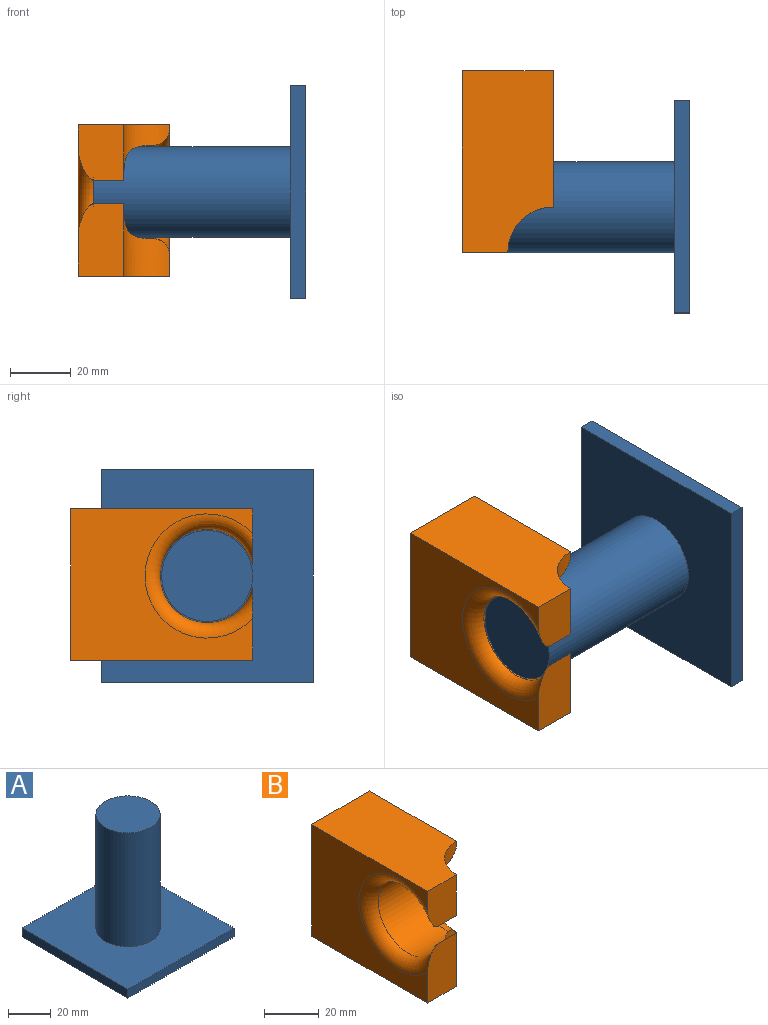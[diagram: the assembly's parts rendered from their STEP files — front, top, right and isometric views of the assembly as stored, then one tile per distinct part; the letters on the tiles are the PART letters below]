
ASSEMBLY  parts=2 mates=1
PART A: 8 faces, bbox 70x70x70 mm
  f0: plane 70x5mm, normal (0,-1,0), area 350mm2, adj f1,f3,f4,f5
  f1: plane 70x5mm, normal (1,0,0), area 350mm2, adj f0,f2,f4,f5
  f2: plane 70x5mm, normal (0,1,0), area 350mm2, adj f1,f3,f4,f5
  f3: plane 70x5mm, normal (-1,0,0), area 350mm2, adj f0,f2,f4,f5
  f4: plane 70x70mm, normal (0,0,1), area 4193.1mm2, adj f0,f1,f2,f3,f6
  f5: plane 70x70mm, normal (0,0,-1), area 4900mm2, adj f0,f1,f2,f3
  f6: cylinder r=15mm len=65mm, axis (0,0,-1), area 6126.1mm2, adj f4,f7
  f7: plane 30x30mm, normal (0,0,1), area 706.9mm2, adj f6
PART B: 12 faces, bbox 30x70.2x53.9 mm
  f0: cylinder r=15mm len=18.27mm, axis (0,0,-1), area 199.7mm2, adj f1,f2,f7,f9,f11
  f1: plane 50x45mm, normal (1,0,0), area 1589.9mm2, adj f0,f3,f4,f7,f8,f11
  f2: plane 18.27x15mm, normal (0,-1,0), area 260.1mm2, adj f0,f5,f7,f9,f10
  f3: cylinder r=15mm len=23.92mm, axis (0,0,-1), area 332.8mm2, adj f1,f6,f8,f9,f11
  f4: plane 50x30mm, normal (0,1,0), area 1500mm2, adj f1,f5,f7,f8
  f5: plane 60x50mm, normal (-1,0,0), area 1785.3mm2, adj f2,f4,f6,f7,f8,f10
  f6: plane 23.92x15mm, normal (0,-1,0), area 344.9mm2, adj f3,f5,f8,f9,f10
  f7: plane 60x30mm, normal (0,0,1), area 1623.3mm2, adj f0,f1,f2,f4,f5
  f8: plane 60x30mm, normal (0,0,-1), area 1623.3mm2, adj f1,f3,f4,f5,f6
  f9: cylinder r=15.5mm len=31mm, axis (1,0,0), area 1480.7mm2, adj f0,f2,f3,f6,f10,f11
  f10: torus R=20.5mm, axis (-1,0,0), area 718.4mm2, adj f2,f5,f6,f9
  f11: torus R=20.5mm, axis (-1,0,0), area 430.3mm2, adj f0,f1,f3,f9
PLACE A rot(axis=(0,-1,0),90deg) t=(49.75,-21.28,34.13)mm
PLACE B at identity
MATE revolute A.f6 <-> B.f9  axis (-1,0,0) through (-20.25,-13.93,27.82)mm
